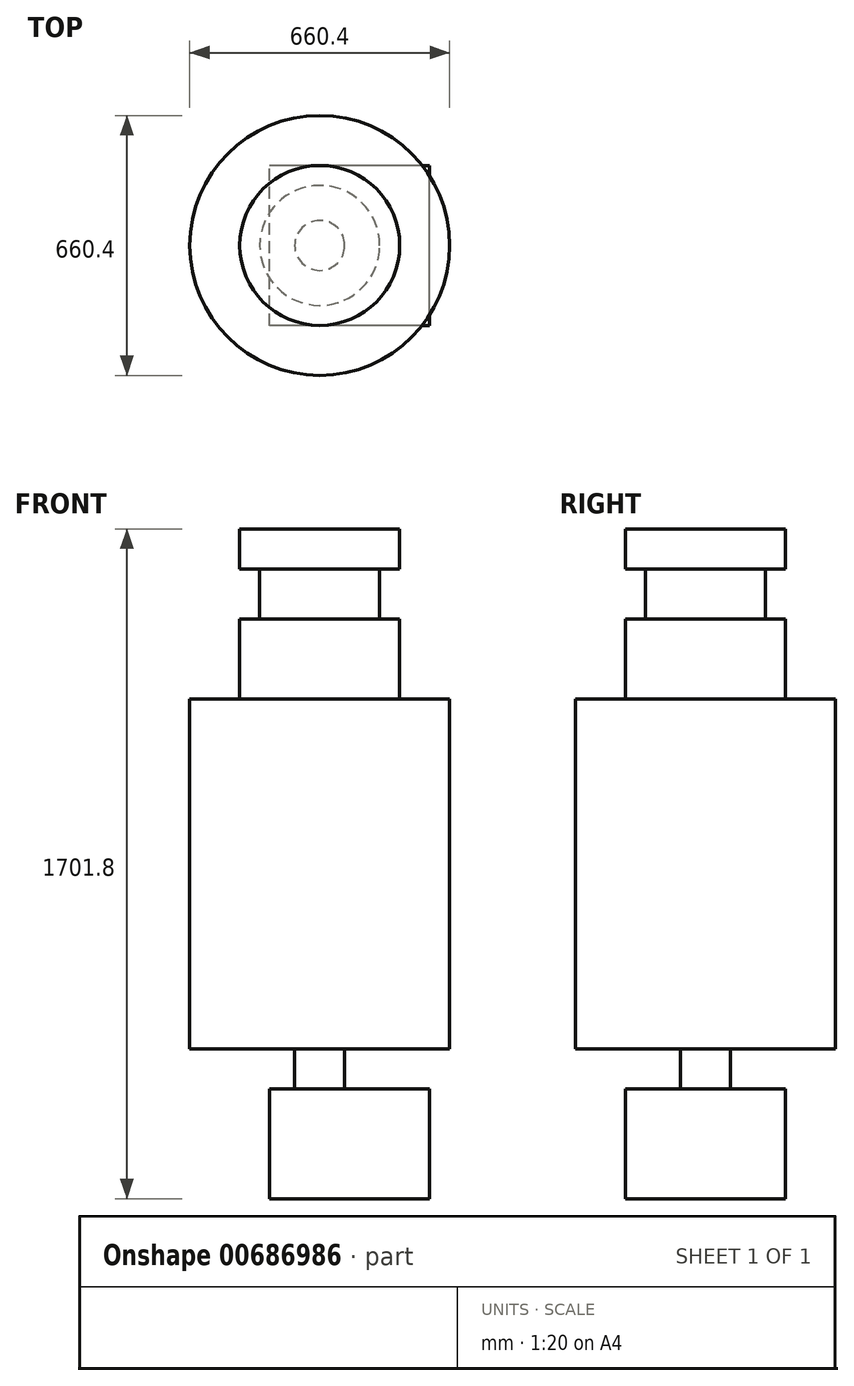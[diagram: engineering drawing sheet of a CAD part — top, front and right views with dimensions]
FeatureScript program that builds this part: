
annotation { "Feature Type Name" : "Feature", "Feature Type Description" : "" }
export const myFeature = defineFeature(function(context is Context, id is Id, definition is map)
    precondition{}
    {
        {
            var Q0;
            Q0=qCreatedBy(makeId("Top.planeOp"),FACE);
            var sketch = newSketch(context, id + "F0", { "sketchPlane" : qUnion([Q0])});
            skCircle(sketch, "E0", {"center": v(0, 0) * mm, "radius": 203.2 * mm});
            skSolve(sketch);
        }
        {
            var Q0;
            Q0 = qSketchRegion(id + "F0", true);
            extrude(context, id + "F1", {"entities" : qUnion([Q0]), "depth" : 101.6 * mm, "offsetDistance" : 25.4 * mm});
        }
        {
            var Q0;
            Q0=makeQuery(id+"F1.opExtrude","CAP_FACE",FACE,{"disambiguationData":[OSD([sQuery(id+"F0.wireOp",EDGE,"E0")])],"isStart":true});
            var sketch = newSketch(context, id + "F2", { "sketchPlane" : qUnion([Q0])});
            skCircle(sketch, "E1", {"center": v(0, 0) * mm, "radius": 152.4 * mm});
            skSolve(sketch);
        }
        {
            var Q0;
            Q0 = qSketchRegion(id + "F2", true);
            extrude(context, id + "F3", {"entities" : qUnion([Q0]), "operationType" : NewBodyOperationType.ADD, "depth" : 127 * mm, "offsetDistance" : 25.4 * mm});
        }
        {
            var Q0;
            Q0=makeQuery(id+"F3.opExtrude","CAP_FACE",FACE,{"disambiguationData":[OSD([sQuery(id+"F2.wireOp",EDGE,"E1")])],"isStart":false});
            var sketch = newSketch(context, id + "F4", { "sketchPlane" : qUnion([Q0])});
            skCircle(sketch, "E2", {"center": v(0, 0) * mm, "radius": 203.2 * mm});
            skSolve(sketch);
        }
        {
            var Q0;
            Q0 = qSketchRegion(id + "F4", true);
            extrude(context, id + "F5", {"entities" : qUnion([Q0]), "operationType" : NewBodyOperationType.ADD, "depth" : 203.2 * mm, "offsetDistance" : 25.4 * mm});
        }
        {
            var Q0;
            Q0=makeQuery(id+"F5.opExtrude","CAP_FACE",FACE,{"disambiguationData":[OSD([sQuery(id+"F4.wireOp",EDGE,"E2")])],"isStart":false});
            var sketch = newSketch(context, id + "F6", { "sketchPlane" : qUnion([Q0])});
            skCircle(sketch, "E3", {"center": v(0, 0) * mm, "radius": 330.2 * mm});
            skSolve(sketch);
        }
        {
            var Q0;
            Q0 = qSketchRegion(id + "F6", true);
            extrude(context, id + "F7", {"entities" : qUnion([Q0]), "operationType" : NewBodyOperationType.ADD, "depth" : 889 * mm, "offsetDistance" : 25.4 * mm});
        }
        {
            var Q0;
            Q0=makeQuery(id+"F7.opExtrude","CAP_FACE",FACE,{"disambiguationData":[OSD([sQuery(id+"F6.wireOp",EDGE,"E3")])],"isStart":false});
            var sketch = newSketch(context, id + "F8", { "sketchPlane" : qUnion([Q0])});
            skCircle(sketch, "E4", {"center": v(0, 0) * mm, "radius": 63.5 * mm});
            skSolve(sketch);
        }
        {
            var Q0;
            Q0 = qSketchRegion(id + "F8", true);
            extrude(context, id + "F9", {"entities" : qUnion([Q0]), "operationType" : NewBodyOperationType.ADD, "depth" : 101.6 * mm, "offsetDistance" : 25.4 * mm});
        }
        {
            var Q0;
            Q0=makeQuery(id+"F9.opExtrude","CAP_FACE",FACE,{"disambiguationData":[OSD([sQuery(id+"F8.wireOp",EDGE,"E4")])],"isStart":false});
            var sketch = newSketch(context, id + "F10", { "sketchPlane" : qUnion([Q0])});
            skLineSegment(sketch, "E5.bottom", {"start": v(279.4, 203.2) * mm, "end": v(-127, 203.2) * mm});
            skLineSegment(sketch, "E5.top", {"start": v(279.4, -203.2) * mm, "end": v(-127, -203.2) * mm});
            skLineSegment(sketch, "E5.left", {"start": v(279.4, 203.2) * mm, "end": v(279.4, -203.2) * mm});
            skLineSegment(sketch, "E5.right", {"start": v(-127, 203.2) * mm, "end": v(-127, -203.2) * mm});
            skLineSegment(sketch, "E6", {"start": v(-127, 0) * mm, "end": v(279.4, 0) * mm, "construction": true});
            skPoint(sketch, "E7", {"position": v(0, 0) * mm});
            skSolve(sketch);
        }
        {
            var Q0;
            Q0=makeQuery(id+"F10.imprint","IMPRINT",FACE,{"disambiguationData":[TD([[makeQuery(id+"F10.imprint","IMPRINT",EDGE,{"derivedFrom":sQuery(id+"F10.wireOp",EDGE,"E5.bottom")}),1.0]])]});
            var Q1;
            Q1=makeQuery(id+"F10.imprint","IMPRINT",FACE,{"disambiguationData":[TD([[makeQuery(id+"F10.imprint","IMPRINT",EDGE,{"derivedFrom":makeQuery(id+"F9.opExtrude","CAP_EDGE",EDGE,{"disambiguationData":[OSD([sQuery(id+"F8.wireOp",EDGE,"E4")])],"isStart":false})}),1.0]])]});
            extrude(context, id + "F11", {"entities" : qUnion([Q0, Q1]), "operationType" : NewBodyOperationType.ADD, "depth" : 279.4 * mm, "offsetDistance" : 25.4 * mm});
        }
    });
